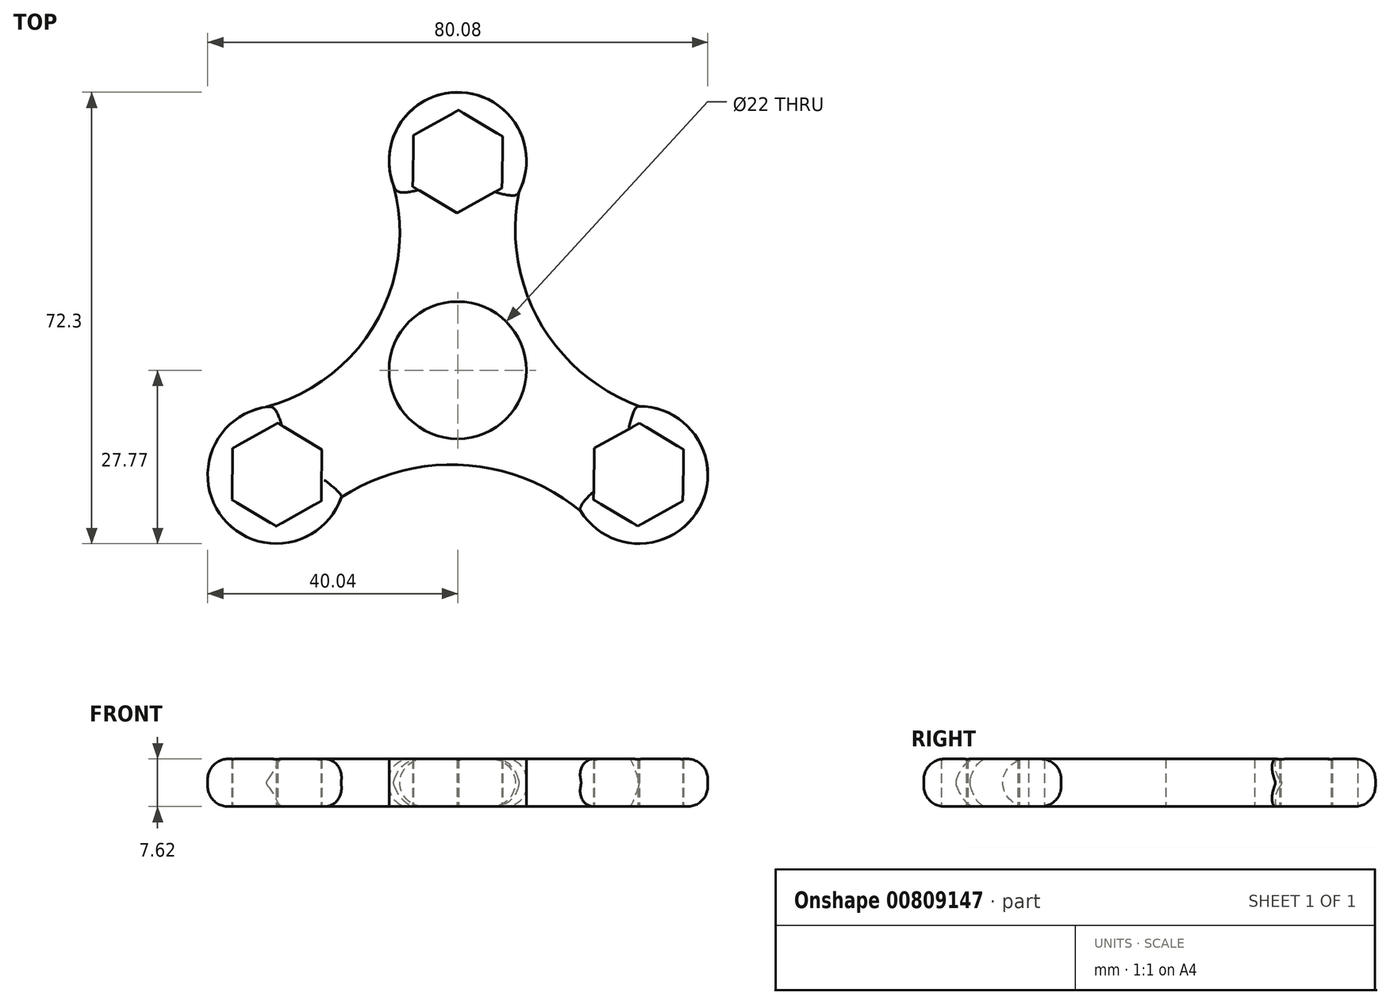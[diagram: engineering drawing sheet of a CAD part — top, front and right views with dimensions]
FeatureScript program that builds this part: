
annotation { "Feature Type Name" : "Feature", "Feature Type Description" : "" }
export const myFeature = defineFeature(function(context is Context, id is Id, definition is map)
    precondition{}
    {
        {
            var Q0;
            Q0=qCreatedBy(makeId("Top.planeOp"),FACE);
            var sketch = newSketch(context, id + "F0", { "sketchPlane" : qUnion([Q0])});
            skCircle(sketch, "E0", {"center": v(0, 0) * mm, "radius": 11 * mm});
            skCircle(sketch, "E1", {"center": v(0, 0) * mm, "radius": 15 * mm});
            skLineSegment(sketch, "E2.0", {"start": v(7.08, 29.2) * mm, "end": v(-0.12, 25.18) * mm});
            skLineSegment(sketch, "E2.1", {"start": v(-0.12, 25.18) * mm, "end": v(-7.2, 29.4) * mm});
            skLineSegment(sketch, "E2.2", {"start": v(-7.2, 29.4) * mm, "end": v(-7.08, 37.66) * mm});
            skLineSegment(sketch, "E2.3", {"start": v(-7.08, 37.66) * mm, "end": v(0.12, 41.68) * mm});
            skLineSegment(sketch, "E2.4", {"start": v(0.12, 41.68) * mm, "end": v(7.2, 37.45) * mm});
            skLineSegment(sketch, "E2.5", {"start": v(7.2, 37.45) * mm, "end": v(7.08, 29.2) * mm});
            skLineSegment(sketch, "E3.1.0", {"start": v(-28.83, -8.47) * mm, "end": v(-21.75, -12.7) * mm});
            skLineSegment(sketch, "E3.1.1", {"start": v(-36.03, -12.49) * mm, "end": v(-28.83, -8.47) * mm});
            skLineSegment(sketch, "E3.1.2", {"start": v(-36.15, -20.74) * mm, "end": v(-36.03, -12.49) * mm});
            skLineSegment(sketch, "E3.1.3", {"start": v(-29.07, -24.96) * mm, "end": v(-36.15, -20.74) * mm});
            skLineSegment(sketch, "E3.1.4", {"start": v(-21.87, -20.94) * mm, "end": v(-29.07, -24.96) * mm});
            skLineSegment(sketch, "E3.1.5", {"start": v(-21.75, -12.7) * mm, "end": v(-21.87, -20.94) * mm});
            skLineSegment(sketch, "E3.2.0", {"start": v(21.75, -20.74) * mm, "end": v(21.87, -12.49) * mm});
            skLineSegment(sketch, "E3.2.1", {"start": v(28.83, -24.96) * mm, "end": v(21.75, -20.74) * mm});
            skLineSegment(sketch, "E3.2.2", {"start": v(36.03, -20.94) * mm, "end": v(28.83, -24.96) * mm});
            skLineSegment(sketch, "E3.2.3", {"start": v(36.15, -12.7) * mm, "end": v(36.03, -20.94) * mm});
            skLineSegment(sketch, "E3.2.4", {"start": v(29.07, -8.47) * mm, "end": v(36.15, -12.7) * mm});
            skLineSegment(sketch, "E3.2.5", {"start": v(21.87, -12.49) * mm, "end": v(29.07, -8.47) * mm});
            skCircle(sketch, "E4", {"center": v(0, 33.53) * mm, "radius": 11 * mm});
            skPoint(sketch, "E4.centerSnap0", {"position": v(-7.14, 33.53) * mm});
            skCircle(sketch, "E5.1.0", {"center": v(-29.04, -16.77) * mm, "radius": 11 * mm});
            skCircle(sketch, "E5.2.0", {"center": v(29.04, -16.77) * mm, "radius": 11 * mm});
            skArc(sketch, "E6", {"start": v(9.78, 28.5) * mm, "mid": v(13.1, 7.8) * mm, "end": v(29.09, -5.77) * mm});
            skArc(sketch, "E7", {"start": v(19.74, -22.64) * mm, "mid": v(0.92, -15.16) * mm, "end": v(-18.64, -20.37) * mm});
            skArc(sketch, "E8", {"start": v(-30.66, -5.89) * mm, "mid": v(-13.13, 7.62) * mm, "end": v(-10.26, 29.56) * mm});
            skSolve(sketch);
        }
        {
            var Q0;
            Q0=makeQuery(id+"F0.imprint","IMPRINT",FACE,{"disambiguationData":[TD([[makeQuery(id+"F0.imprint","IMPRINT",EDGE,{"derivedFrom":sQuery(id+"F0.wireOp",EDGE,"E1")}),-1.0]])]});
            var Q1;
            Q1=makeQuery(id+"F0.imprint","IMPRINT",FACE,{"disambiguationData":[TD([[makeQuery(id+"F0.imprint","IMPRINT",EDGE,{"derivedFrom":sQuery(id+"F0.wireOp",EDGE,"E2.0")}),1.0]])]});
            var Q2;
            Q2=makeQuery(id+"F0.imprint","IMPRINT",FACE,{"disambiguationData":[TD([[makeQuery(id+"F0.imprint","IMPRINT",EDGE,{"derivedFrom":sQuery(id+"F0.wireOp",EDGE,"E3.1.0")}),1.0]])]});
            var Q3;
            Q3=makeQuery(id+"F0.imprint","IMPRINT",FACE,{"disambiguationData":[TD([[makeQuery(id+"F0.imprint","IMPRINT",EDGE,{"derivedFrom":sQuery(id+"F0.wireOp",EDGE,"E3.2.0")}),1.0]])]});
            var Q4;
            Q4=makeQuery(id+"F0.imprint","IMPRINT",FACE,{"disambiguationData":[TD([[makeQuery(id+"F0.imprint","IMPRINT",EDGE,{"derivedFrom":sQuery(id+"F0.wireOp",EDGE,"E0")}),-1.0]])]});
            extrude(context, id + "F1", {"entities" : qUnion([Q0, Q1, Q2, Q3, Q4]), "depth" : 7.62 * mm, "offsetDistance" : 25.4 * mm});
        }
        {
            var Q0;
            Q0=makeQuery(id+"F1.opExtrude","CAP_EDGE",EDGE,{"disambiguationData":[OSD([sQuery(id+"F0.wireOp",EDGE,"E8")])],"isStart":false});
            fillet(context, id + "F2", {"entities" : qUnion([Q0]), "radius" : 3.8 * mm, "tangentPropagation" : true, "allowEdgeOverflow" : false});
        }
        {
            var Q0;
            Q0=makeQuery(id+"F1.opExtrude","CAP_EDGE",EDGE,{"disambiguationData":[OSD([sQuery(id+"F0.wireOp",EDGE,"E7")])],"isStart":false});
            fillet(context, id + "F3", {"entities" : qUnion([Q0]), "radius" : 3.8 * mm, "tangentPropagation" : true, "allowEdgeOverflow" : false});
        }
        {
            var Q0;
            Q0=makeQuery(id+"F1.opExtrude","CAP_EDGE",EDGE,{"disambiguationData":[OSD([sQuery(id+"F0.wireOp",EDGE,"E6")])],"isStart":false});
            fillet(context, id + "F4", {"entities" : qUnion([Q0]), "radius" : 3.8 * mm, "tangentPropagation" : true, "allowEdgeOverflow" : false});
        }
        {
            var Q0;
            Q0=makeQuery(id+"F1.opExtrude","CAP_EDGE",EDGE,{"disambiguationData":[OSD([sQuery(id+"F0.wireOp",EDGE,"E7")])],"isStart":true});
            fillet(context, id + "F5", {"entities" : qUnion([Q0]), "radius" : 3.8 * mm, "tangentPropagation" : true, "allowEdgeOverflow" : false});
        }
        {
            var Q0;
            Q0=makeQuery(id+"F1.opExtrude","CAP_EDGE",EDGE,{"disambiguationData":[OSD([sQuery(id+"F0.wireOp",EDGE,"E6")])],"isStart":true});
            var Q1;
            Q1=makeQuery(id+"F1.opExtrude","CAP_EDGE",EDGE,{"disambiguationData":[OSD([sQuery(id+"F0.wireOp",EDGE,"E8")])],"isStart":true});
            fillet(context, id + "F6", {"entities" : qUnion([Q0, Q1]), "radius" : 3.8 * mm, "tangentPropagation" : true, "allowEdgeOverflow" : false});
        }
        {
            var Q0;
            Q0=makeQuery(id+"F1.opExtrude","CAP_EDGE",EDGE,{"disambiguationData":[OSD([sQuery(id+"F0.wireOp",EDGE,"E5.1.0")])],"isStart":true});
            fillet(context, id + "F7", {"entities" : qUnion([Q0]), "radius" : 3.28 * mm, "tangentPropagation" : true, "allowEdgeOverflow" : false});
        }
        {
            var Q0;
            Q0=makeQuery(id+"F1.opExtrude","CAP_EDGE",EDGE,{"disambiguationData":[OSD([sQuery(id+"F0.wireOp",EDGE,"E4")])],"isStart":true});
            var Q1;
            Q1=makeQuery(id+"F1.opExtrude","CAP_EDGE",EDGE,{"disambiguationData":[OSD([sQuery(id+"F0.wireOp",EDGE,"E5.2.0")])],"isStart":true});
            fillet(context, id + "F8", {"entities" : qUnion([Q0, Q1]), "radius" : 3.28 * mm, "tangentPropagation" : true, "allowEdgeOverflow" : false});
        }
        {
            var Q0;
            Q0=makeQuery(id+"F1.opExtrude","CAP_EDGE",EDGE,{"disambiguationData":[OSD([sQuery(id+"F0.wireOp",EDGE,"E4")])],"isStart":false});
            var Q1;
            Q1=makeQuery(id+"F1.opExtrude","CAP_EDGE",EDGE,{"disambiguationData":[OSD([sQuery(id+"F0.wireOp",EDGE,"E5.2.0")])],"isStart":false});
            var Q2;
            Q2=makeQuery(id+"F1.opExtrude","CAP_EDGE",EDGE,{"disambiguationData":[OSD([sQuery(id+"F0.wireOp",EDGE,"E5.1.0")])],"isStart":false});
            fillet(context, id + "F9", {"entities" : qUnion([Q0, Q1, Q2]), "radius" : 3.28 * mm, "tangentPropagation" : true, "allowEdgeOverflow" : false});
        }
    });
